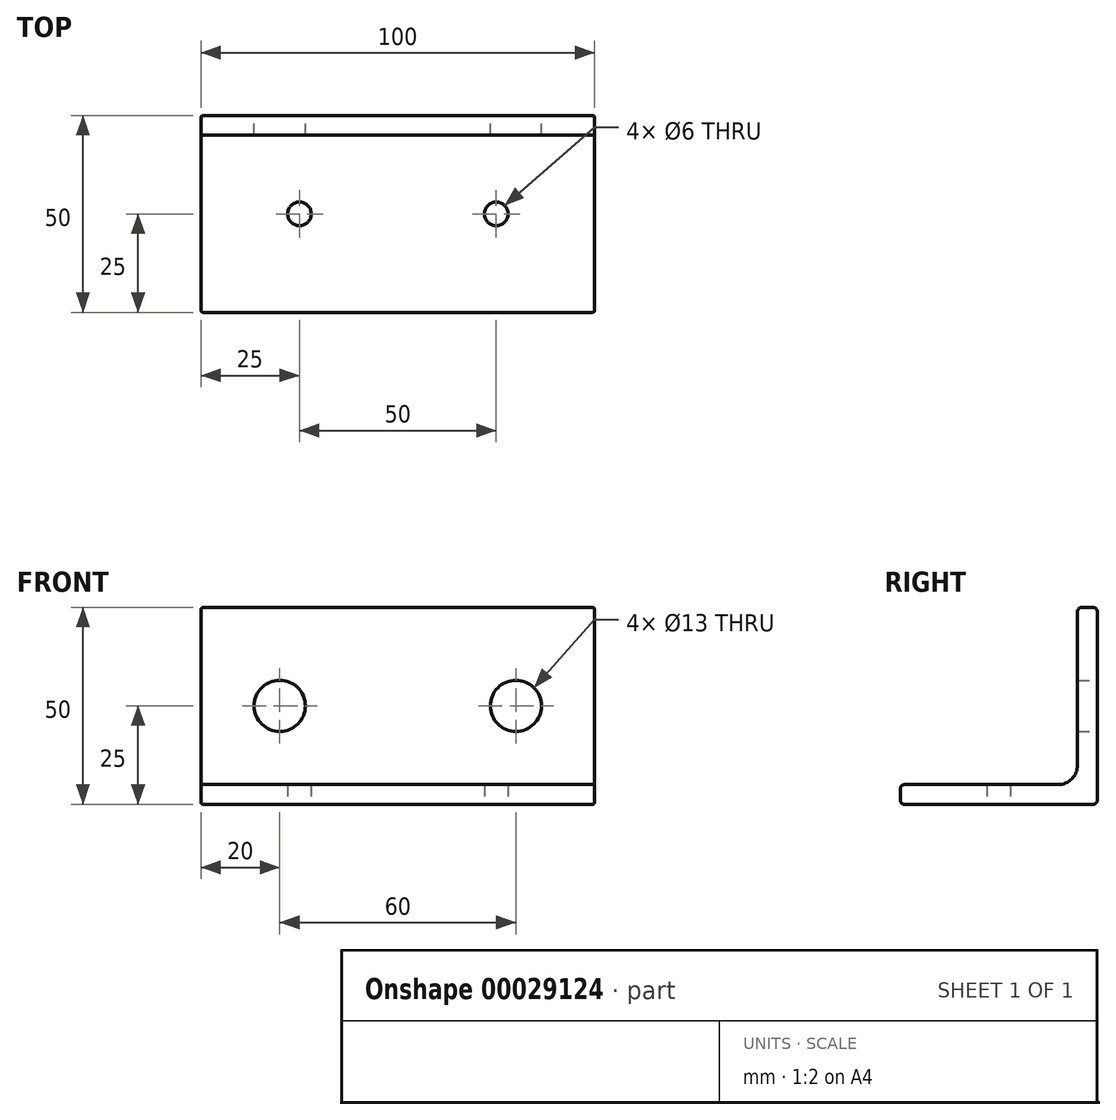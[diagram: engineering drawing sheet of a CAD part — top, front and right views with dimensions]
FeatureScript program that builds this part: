
annotation { "Feature Type Name" : "Feature", "Feature Type Description" : "" }
export const myFeature = defineFeature(function(context is Context, id is Id, definition is map)
    precondition{}
    {
        {
            var Q0;
            Q0=qCreatedBy(makeId("Right.planeOp"),FACE);
            var sketch = newSketch(context, id + "F0", { "sketchPlane" : qUnion([Q0])});
            skLineSegment(sketch, "E0", {"start": v(-49, 0) * mm, "end": v(-1, 0) * mm});
            skLineSegment(sketch, "E1", {"start": v(0, 1) * mm, "end": v(0, 49) * mm});
            skLineSegment(sketch, "E2", {"start": v(-1, 50) * mm, "end": v(-4, 50) * mm});
            skLineSegment(sketch, "E3", {"start": v(-5, 49) * mm, "end": v(-5, 10) * mm});
            skLineSegment(sketch, "E4", {"start": v(-10, 5) * mm, "end": v(-49, 5) * mm});
            skLineSegment(sketch, "E5", {"start": v(-50, 4) * mm, "end": v(-50, 1) * mm});
            skPoint(sketch, "E6.visualSharp", {"position": v(-5, 5) * mm});
            skArc(sketch, "E6.filletArc", {"start": v(-10, 5) * mm, "mid": v(-6.46, 6.46) * mm, "end": v(-5, 10) * mm});
            skPoint(sketch, "E7.visualSharp", {"position": v(0, 50) * mm});
            skArc(sketch, "E7.filletArc", {"start": v(0, 49) * mm, "mid": v(-0.3, 49.7) * mm, "end": v(-1, 50) * mm});
            skPoint(sketch, "E8.visualSharp", {"position": v(-5, 50) * mm});
            skArc(sketch, "E8.filletArc", {"start": v(-4, 50) * mm, "mid": v(-4.7, 49.7) * mm, "end": v(-5, 49) * mm});
            skPoint(sketch, "E9.visualSharp", {"position": v(-50, 5) * mm});
            skArc(sketch, "E9.filletArc", {"start": v(-49, 5) * mm, "mid": v(-49.7, 4.7) * mm, "end": v(-50, 4) * mm});
            skPoint(sketch, "E10.visualSharp", {"position": v(-50, 0) * mm});
            skArc(sketch, "E10.filletArc", {"start": v(-50, 1) * mm, "mid": v(-49.7, 0.3) * mm, "end": v(-49, 0) * mm});
            skPoint(sketch, "E11.visualSharp", {"position": v(0, 0) * mm});
            skArc(sketch, "E11.filletArc", {"start": v(-1, 0) * mm, "mid": v(-0.3, 0.3) * mm, "end": v(0, 1) * mm});
            skSolve(sketch);
        }
        {
            var Q0;
            Q0 = qSketchRegion(id + "F0", true);
            extrude(context, id + "F1", {"entities" : qUnion([Q0]), "endBound" : BoundingType.SYMMETRIC, "depth" : 100 * mm});
        }
        {
            var Q0;
            Q0=makeQuery(id+"F1.opExtrude","SWEPT_FACE",FACE,{"disambiguationData":[OSD([sQuery(id+"F0.wireOp",EDGE,"E1")])]});
            var sketch = newSketch(context, id + "F2", { "sketchPlane" : qUnion([Q0])});
            skLineSegment(sketch, "E12.0", {"start": v(-50, 50) * mm, "end": v(50, 50) * mm, "construction": true});
            skLineSegment(sketch, "E12.1", {"start": v(-50, 0) * mm, "end": v(50, 0) * mm, "construction": true});
            skLineSegment(sketch, "E13", {"start": v(-50, 25) * mm, "end": v(-30, 25) * mm, "construction": true});
            skLineSegment(sketch, "E14", {"start": v(50, 25) * mm, "end": v(30, 25) * mm, "construction": true});
            skCircle(sketch, "E15", {"center": v(-30, 25) * mm, "radius": 6.5 * mm});
            skCircle(sketch, "E16", {"center": v(30, 25) * mm, "radius": 6.5 * mm});
            skSolve(sketch);
        }
        {
            var Q0;
            Q0=makeQuery(id+"F2.imprint","IMPRINT",FACE,{"disambiguationData":[TD([[makeQuery(id+"F2.imprint","IMPRINT",EDGE,{"derivedFrom":sQuery(id+"F2.wireOp",EDGE,"E15")}),1.0]])]});
            var Q1;
            Q1=makeQuery(id+"F2.imprint","IMPRINT",FACE,{"disambiguationData":[TD([[makeQuery(id+"F2.imprint","IMPRINT",EDGE,{"derivedFrom":sQuery(id+"F2.wireOp",EDGE,"E16")}),1.0]])]});
            extrude(context, id + "F3", {"entities" : qUnion([Q0, Q1]), "operationType" : NewBodyOperationType.REMOVE, "endBound" : BoundingType.THROUGH_ALL, "oppositeDirection" : true, "depth" : 25 * mm});
        }
        {
            var Q0;
            Q0=makeQuery(id+"F1.opExtrude","SWEPT_FACE",FACE,{"disambiguationData":[OSD([sQuery(id+"F0.wireOp",EDGE,"E0")])]});
            var sketch = newSketch(context, id + "F4", { "sketchPlane" : qUnion([Q0])});
            skLineSegment(sketch, "E17", {"start": v(50, 25) * mm, "end": v(25, 25) * mm, "construction": true});
            skLineSegment(sketch, "E18", {"start": v(-50, 25) * mm, "end": v(-25, 25) * mm, "construction": true});
            skCircle(sketch, "E19", {"center": v(25, 25) * mm, "radius": 3 * mm});
            skCircle(sketch, "E20", {"center": v(-25, 25) * mm, "radius": 3 * mm});
            skSolve(sketch);
        }
        {
            var Q0;
            Q0=makeQuery(id+"F4.imprint","IMPRINT",FACE,{"disambiguationData":[TD([[makeQuery(id+"F4.imprint","IMPRINT",EDGE,{"derivedFrom":sQuery(id+"F4.wireOp",EDGE,"E19")}),1.0]])]});
            var Q1;
            Q1=makeQuery(id+"F4.imprint","IMPRINT",FACE,{"disambiguationData":[TD([[makeQuery(id+"F4.imprint","IMPRINT",EDGE,{"derivedFrom":sQuery(id+"F4.wireOp",EDGE,"E20")}),1.0]])]});
            extrude(context, id + "F5", {"entities" : qUnion([Q0, Q1]), "operationType" : NewBodyOperationType.REMOVE, "endBound" : BoundingType.THROUGH_ALL, "oppositeDirection" : true, "depth" : 25 * mm});
        }
        {
            var Q0;
            Q0=makeQuery(id+"F1.opExtrude","CAP_EDGE",EDGE,{"disambiguationData":[OSD([sQuery(id+"F0.wireOp",EDGE,"E4")])],"isStart":false});
            var Q1;
            Q1=makeQuery(id+"F1.opExtrude","CAP_EDGE",EDGE,{"disambiguationData":[OSD([sQuery(id+"F0.wireOp",EDGE,"E4")])],"isStart":true});
            fillet(context, id + "F6", {"entities" : qUnion([Q0, Q1]), "radius" : 0.5 * mm, "tangentPropagation" : true, "allowEdgeOverflow" : false});
        }
    });
